# Revit family: Zumtobel AMPHIBIA Round
name_source: partatom
category: Lighting Fixtures
revit_build: Autodesk Revit 2016 (Build: 20150220_1215(x64)
units: mm (PartAtom-declared; Revit-internal decimal feet)

## family parameters
Cut with Voids When Loaded = No
Host = Face
Light Source = Yes
OmniClass Number = 23.80.70.11
OmniClass Title = Luminaries for Internal Lighting
Part Type = Normal
Room Calculation Point = No
Round Connector Dimension = Use Diameter
Shared = No

## types (2) — shared parameters
Assembly Code = D5020210
Body = ZG_PMMA_Semitransparent
Color Filter = 16777215
Cover = ZG_PMMA_Semitransparent_SI
Description = Moisture-proof diffuser luminaire
Dimming Lamp Color Temperature Shift = <None>
Emit Shape Visible in Rendering = No
Lamp = LED
Manufacturer = Zumtobel Lighting
RL = No
RS = Yes
Tilt Angle = -90.00°
URL = http://www.zumtobel.com
Voltage = 230 V
zero-valued in all types: Default Elevation

## per-type parameters (varying)
| type | Apparent Load | Emit from Circle Diameter | Height | Length | Model | Photometric Web File | Width |
| AMP RS 3000-840 LDO KST | 24 VA | 247 mm | 124 mm | 395 mm | 42186498 | 42186498_(STD_LEO).IES | 395 mm |
| AMP RL 5600-840 LDO V2A | 47 VA | 524 mm  [stored 1.71916 ft] | 146 mm | 690 mm | 42186504 | 42186504_(STD_LEO).IES | 690 mm |

note: [stored X ft] marks values corroborated as IEEE doubles in the binary element streams (Revit-internal decimal feet)

## geometry (parser evidence)
native form markers: Sweep x3
no freeform markers — native parametric forms only
